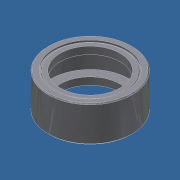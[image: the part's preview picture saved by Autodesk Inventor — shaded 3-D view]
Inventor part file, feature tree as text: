
AUTODESK INVENTOR PART (.ipt)
format: ipt  version: unknown  size: 244,736 bytes
history: native  units: in
note: dims shown in document units (in); Inventor stores cm internally (conversion verified against a paired STEP export)
features: sketch x6, extrude x5, chamfer x4, plane x3, revolve x1
ambient origin geometry x8: Origin, YZ Plane, XZ Plane, XY Plane, X Axis, Y Axis, Z Axis, Center Point
bodies: Solid1 (feature_tree)
feature tree (19):
  revolve  "Revolution1"  [1 undecoded]
  plane  "Work Plane1"
  extrude  "Extrusion1"  TaperAngle=90.0deg  [1 undecoded]
  plane  "Work Plane2"
  extrude  "Extrusion2"  Depth=0.626in
  plane  "Work Plane3"
  extrude  "Extrusion3"  [1 undecoded]
  extrude  "Extrusion4"  Depth=0.0756in TaperAngle=0.0deg
  chamfer  "Chamfer1"  Distance=0.815in
  extrude  "Extrusion5"  Depth=0.2018in TaperAngle=0.0deg
  chamfer  "Chamfer2"  Distance=0.01in
  chamfer  "Chamfer3"  Distance=0.01in
  chamfer  "Chamfer4"  Distance=0.01in Angle=45.0deg
  sketch  "Sketch1"  dims[d0=0.373in d1=0.06in]
  sketch  "Sketch2"  dims[d2=0.4375in d3=90.0deg]
  sketch  "Sketch3"  dims[d4=-0.01in d5=0.626in]
  sketch  "Sketch4"  dims[d6=0.0756in d7=0.0in d8=-0.01in]
  sketch  "Sketch5"  dims[d9=0.626in d10=0.0756in d11=0.0in]
  sketch  "Sketch6"  dims[d12=0.0in d13=0.815in d14=0.2018in d15=0.0in d16=0.01in d17=0.01in d18=0.0in d19=0.01in d20=0.125in d21=45.0deg d22=0.01in d23=0.01in d24=0.0in d25=0.01in d26=0.125in d27=45.0deg d28=0.01in d29=0.125in d30=45.0deg d31=0.01in d32=0.125in d33=45.0deg d34=0.875in d35=0.875in]
note: 3 required parameter values undecoded (feature->parameter linkage not recoverable at this tier; creation-order binding heuristic only, values carry confidence <= 0.55)